# Revit family: rba-bim-B38034
name_source: partatom
category: Specialty Equipment
revit_build: Autodesk Revit 2018 (Build: 20170223_1515(x64)
units: mm (PartAtom-declared; Revit-internal decimal feet)

## family parameters
Cut with Voids When Loaded = No
Host = Face
OmniClass Number = 23.40.20.21.17
OmniClass Title = Paper Towel Dispensers, Disposal Units
Part Type = Normal
Room Calculation Point = No
Round Connector Dimension = Use Diameter
Shared = Yes

## types (1)
- B-38034
    ADA Compliant = Yes
    Assembly Code = C1030200
    Default Elevation = 1.219
    Description = Recessed Paper Towel Dispenser And Waste Receptacle
    Manufacturer = Bobrick Washroom Equipment
    Materials and Finishes = Stainless Steel Satin Finish
    Model = B38034
    Modified Issue = 20200831.01
    Product Name = Recessed Paper Towel Dispenser And Waste Receptacle
    Type Comments = Satin Finish
    URL = www.rba.com.au

## geometry (parser evidence)
native form markers: Blend x12, Sweep x1
no freeform markers — native parametric forms only
